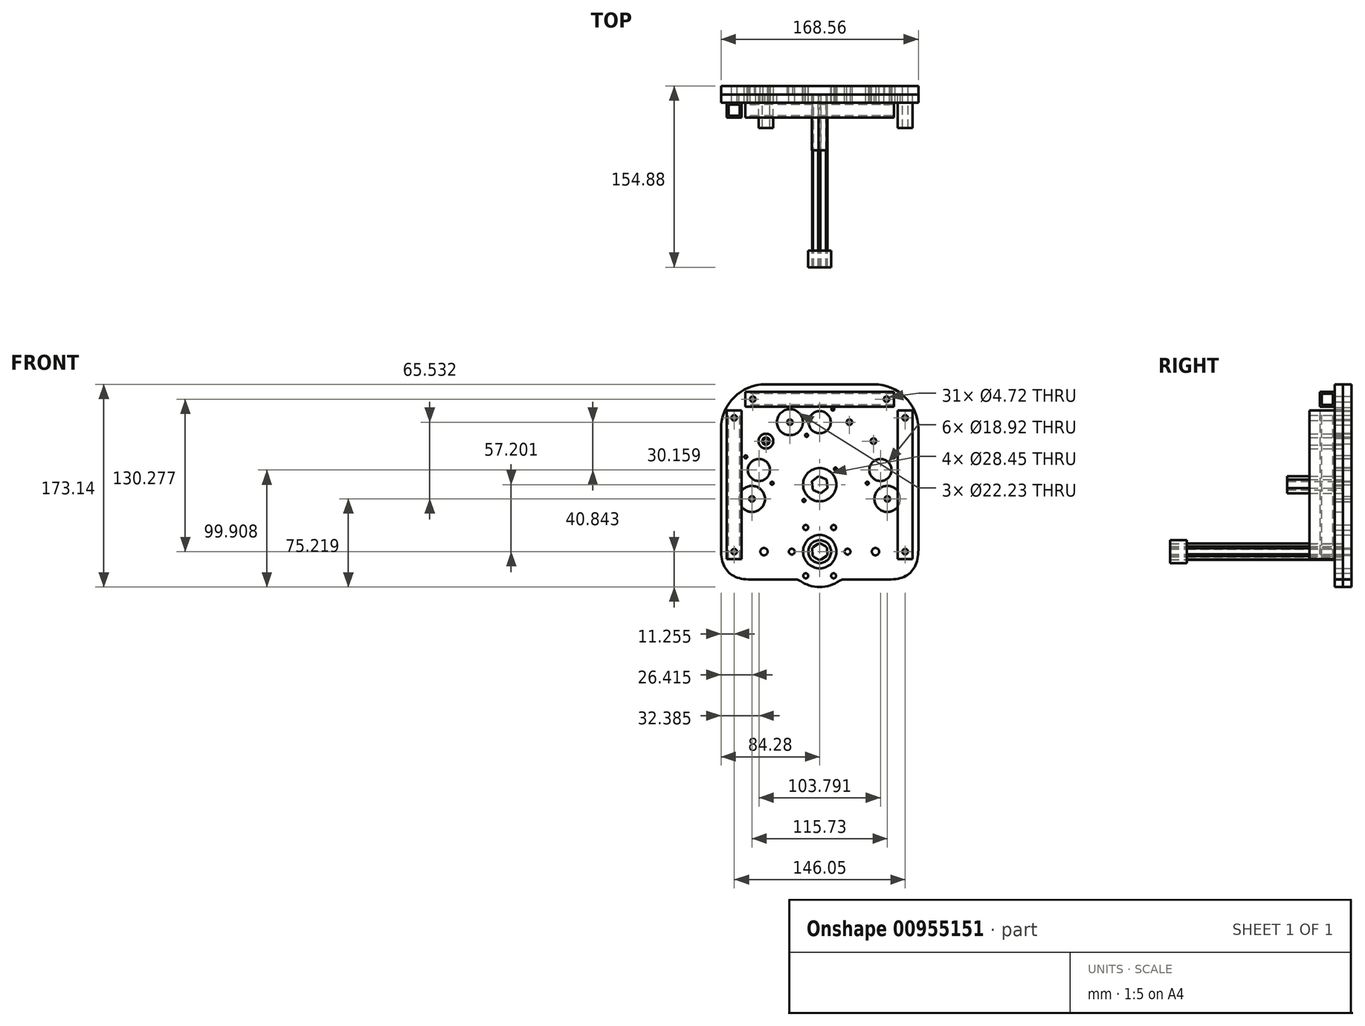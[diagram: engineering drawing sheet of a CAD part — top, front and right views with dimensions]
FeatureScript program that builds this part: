
annotation { "Feature Type Name" : "Feature", "Feature Type Description" : "" }
export const myFeature = defineFeature(function(context is Context, id is Id, definition is map)
    precondition{}
    {
        {
            var Q0;
            Q0=qCreatedBy(makeId("Front.planeOp"),FACE);
            var sketch = newSketch(context, id + "F0", { "sketchPlane" : qUnion([Q0])});
            skPoint(sketch, "E0.middle", {"position": v(0, 0) * mm});
            skCircle(sketch, "E1", {"center": v(0, 53.4) * mm, "radius": 9.46 * mm});
            skCircle(sketch, "E2", {"center": v(-51.9, 12.55) * mm, "radius": 9.46 * mm});
            skCircle(sketch, "E3", {"center": v(0, 0) * mm, "radius": 14.22 * mm});
            skCircle(sketch, "E4", {"center": v(0, -57.2) * mm, "radius": 14.22 * mm});
            skCircle(sketch, "E5", {"center": v(-25.4, 53.4) * mm, "radius": 2.36 * mm});
            skLineSegment(sketch, "E6", {"start": v(0, 0) * mm, "end": v(-51.9, 12.55) * mm, "construction": true});
            skLineSegment(sketch, "E7", {"start": v(-45.93, 37.24) * mm, "end": v(-57.86, -12.14) * mm, "construction": true});
            skCircle(sketch, "E8", {"center": v(-45.93, 37.24) * mm, "radius": 2.36 * mm});
            skCircle(sketch, "E9", {"center": v(-57.86, -12.14) * mm, "radius": 2.36 * mm});
            skCircle(sketch, "E10.MirrorC", {"center": v(45.93, 37.24) * mm, "radius": 2.36 * mm});
            skCircle(sketch, "E11.MirrorC", {"center": v(57.86, -12.14) * mm, "radius": 2.36 * mm});
            skCircle(sketch, "E12.MirrorC", {"center": v(25.4, 53.4) * mm, "radius": 2.36 * mm});
            skCircle(sketch, "E13.MirrorC", {"center": v(51.9, 12.55) * mm, "radius": 9.46 * mm});
            skCircle(sketch, "E14", {"center": v(-47.63, -57.2) * mm, "radius": 3.11 * mm});
            skCircle(sketch, "E15.MirrorC", {"center": v(47.63, -57.2) * mm, "radius": 3.11 * mm});
            skLineSegment(sketch, "E16", {"start": v(-25.4, 53.4) * mm, "end": v(25.4, 53.4) * mm, "construction": true});
            skCircle(sketch, "E17", {"center": v(0, 53.4) * mm, "radius": 32.39 * mm, "construction": true});
            skCircle(sketch, "E18", {"center": v(-51.9, 12.55) * mm, "radius": 32.39 * mm, "construction": true});
            skCircle(sketch, "E19", {"center": v(51.9, 12.55) * mm, "radius": 32.39 * mm, "construction": true});
            skLineSegment(sketch, "E20.bottom", {"start": v(84.28, 85.78) * mm, "end": v(-84.28, 85.78) * mm});
            skLineSegment(sketch, "E20.left", {"start": v(84.28, 85.78) * mm, "end": v(84.28, -81.01) * mm});
            skLineSegment(sketch, "E20.right", {"start": v(-84.28, 85.78) * mm, "end": v(-84.28, -81.01) * mm});
            skCircle(sketch, "E21", {"center": v(-73.03, 57.1) * mm, "radius": 2.36 * mm});
            skCircle(sketch, "E22.MirrorC", {"center": v(73.03, 57.1) * mm, "radius": 2.36 * mm});
            skCircle(sketch, "E23", {"center": v(-73.03, -57.2) * mm, "radius": 2.36 * mm});
            skCircle(sketch, "E24.MirrorC", {"center": v(73.03, -57.2) * mm, "radius": 2.36 * mm});
            skLineSegment(sketch, "E25", {"start": v(-11.23, 42.17) * mm, "end": v(11.23, 64.62) * mm, "construction": true});
            skCircle(sketch, "E26", {"center": v(-11.23, 42.17) * mm, "radius": 1.27 * mm});
            skCircle(sketch, "E27", {"center": v(11.23, 64.62) * mm, "radius": 1.27 * mm});
            skLineSegment(sketch, "E28", {"start": v(-57.15, 73.08) * mm, "end": v(57.15, 73.08) * mm, "construction": true});
            skCircle(sketch, "E29", {"center": v(-57.15, 73.08) * mm, "radius": 2.36 * mm});
            skLineSegment(sketch, "E30", {"start": v(-73.03, 57.1) * mm, "end": v(-73.03, -57.2) * mm, "construction": true});
            skPoint(sketch, "E31", {"position": v(0, 73.08) * mm});
            skCircle(sketch, "E32", {"center": v(57.15, 73.08) * mm, "radius": 2.36 * mm});
            skLineSegment(sketch, "E33", {"start": v(-13.47, -13.47) * mm, "end": v(13.47, 13.47) * mm, "construction": true});
            skCircle(sketch, "E34", {"center": v(13.47, 13.47) * mm, "radius": 1.27 * mm});
            skCircle(sketch, "E35", {"center": v(-13.47, -13.47) * mm, "radius": 1.27 * mm});
            skLineSegment(sketch, "E36", {"start": v(-63.12, 23.77) * mm, "end": v(-40.67, 1.32) * mm, "construction": true});
            skLineSegment(sketch, "E37", {"start": v(40.67, 1.32) * mm, "end": v(63.12, 23.77) * mm, "construction": true});
            skCircle(sketch, "E38", {"center": v(-40.67, 1.32) * mm, "radius": 1.27 * mm});
            skCircle(sketch, "E39", {"center": v(-63.12, 23.77) * mm, "radius": 1.27 * mm});
            skCircle(sketch, "E40", {"center": v(63.12, 23.77) * mm, "radius": 1.27 * mm});
            skCircle(sketch, "E41", {"center": v(40.67, 1.32) * mm, "radius": 1.27 * mm});
            skCircle(sketch, "E42", {"center": v(23.81, -57.2) * mm, "radius": 2.15 * mm});
            skCircle(sketch, "E43.1.0", {"center": v(11.9, -36.58) * mm, "radius": 2.15 * mm});
            skCircle(sketch, "E43.2.0", {"center": v(-11.9, -36.58) * mm, "radius": 2.15 * mm});
            skCircle(sketch, "E43.3.0", {"center": v(-23.81, -57.2) * mm, "radius": 2.15 * mm});
            skCircle(sketch, "E43.4.0", {"center": v(-11.9, -77.82) * mm, "radius": 2.15 * mm});
            skCircle(sketch, "E43.5.0", {"center": v(11.9, -77.82) * mm, "radius": 2.15 * mm});
            skCircle(sketch, "E44", {"center": v(0, -57.2) * mm, "radius": 23.81 * mm, "construction": true});
            skCircle(sketch, "E45.0", {"center": v(0, -57.2) * mm, "radius": 30.16 * mm, "construction": true});
            skLineSegment(sketch, "E46", {"start": v(84.28, -81.01) * mm, "end": v(18.51, -81.01) * mm});
            skLineSegment(sketch, "E47", {"start": v(-84.28, -81.01) * mm, "end": v(-18.51, -81.01) * mm});
            skArc(sketch, "E48", {"start": v(-18.51, -81.01) * mm, "mid": v(0, -87.36) * mm, "end": v(18.51, -81.01) * mm});
            skCircle(sketch, "E49", {"center": v(-23.81, -57.2) * mm, "radius": 2.49 * mm});
            skCircle(sketch, "E50", {"center": v(23.81, -57.2) * mm, "radius": 2.49 * mm});
            skSolve(sketch);
        }
        {
            var Q0;
            Q0=makeQuery(id+"F0.imprint","IMPRINT",FACE,{"disambiguationData":[TD([[makeQuery(id+"F0.imprint","IMPRINT",EDGE,{"derivedFrom":sQuery(id+"F0.wireOp",EDGE,"E1")}),-1.0]])]});
            extrude(context, id + "F1", {"entities" : qUnion([Q0]), "depth" : 7.24 * mm, "offsetDistance" : 25.4 * mm});
        }
        {
            var Q0;
            Q0=makeQuery(id+"F1.opExtrude","CAP_FACE",FACE,{"disambiguationData":[OSD([sQuery(id+"F0.wireOp",EDGE,"E1"),sQuery(id+"F0.wireOp",EDGE,"E2"),sQuery(id+"F0.wireOp",EDGE,"v2gbIf3F-sjIH-0Jlf-8SnF-WHDscdTQMHb3.bottom"),sQuery(id+"F0.wireOp",EDGE,"v2gbIf3F-sjIH-0Jlf-8SnF-WHDscdTQMHb3.top"),sQuery(id+"F0.wireOp",EDGE,"v2gbIf3F-sjIH-0Jlf-8SnF-WHDscdTQMHb3.left"),sQuery(id+"F0.wireOp",EDGE,"v2gbIf3F-sjIH-0Jlf-8SnF-WHDscdTQMHb3.right"),sQuery(id+"F0.wireOp",EDGE,"E3"),sQuery(id+"F0.wireOp",EDGE,"E4"),sQuery(id+"F0.wireOp",EDGE,"E5"),sQuery(id+"F0.wireOp",EDGE,"E8"),sQuery(id+"F0.wireOp",EDGE,"E9"),sQuery(id+"F0.wireOp",EDGE,"E10.MirrorC"),sQuery(id+"F0.wireOp",EDGE,"E11.MirrorC"),sQuery(id+"F0.wireOp",EDGE,"E12.MirrorC"),sQuery(id+"F0.wireOp",EDGE,"9f56034d-28e1-4162-898a-95c3412c0e040.MirrorCS"),sQuery(id+"F0.wireOp",EDGE,"273e83dc-7785-426b-80ec-8bf11da8723f0.MirrorCS"),sQuery(id+"F0.wireOp",EDGE,"E13.MirrorC")])],"isStart":false});
            var sketch = newSketch(context, id + "F2", { "sketchPlane" : qUnion([Q0])});
            skCircle(sketch, "E51", {"center": v(-45.93, 37.24) * mm, "radius": 6.35 * mm});
            skCircle(sketch, "E52", {"center": v(-45.93, 37.24) * mm, "radius": 3.18 * mm});
            skSolve(sketch);
        }
        {
            var Q0;
            Q0=qSketchRegion(id+"F2",true);
            extrude(context, id + "F3", {"entities" : qUnion([Q0]), "depth" : 28.75 * mm, "offsetDistance" : 25.4 * mm});
        }
        {
            var Q0;
            Q0=makeQuery(id+"F1.opExtrude","CAP_FACE",FACE,{"disambiguationData":[OSD([sQuery(id+"F0.wireOp",EDGE,"E1"),sQuery(id+"F0.wireOp",EDGE,"E2"),sQuery(id+"F0.wireOp",EDGE,"E3"),sQuery(id+"F0.wireOp",EDGE,"E4"),sQuery(id+"F0.wireOp",EDGE,"E5"),sQuery(id+"F0.wireOp",EDGE,"E8"),sQuery(id+"F0.wireOp",EDGE,"E9"),sQuery(id+"F0.wireOp",EDGE,"E10.MirrorC"),sQuery(id+"F0.wireOp",EDGE,"E11.MirrorC"),sQuery(id+"F0.wireOp",EDGE,"E12.MirrorC"),sQuery(id+"F0.wireOp",EDGE,"E13.MirrorC"),sQuery(id+"F0.wireOp",EDGE,"jZPg6kl5-KOBd-NjPk-bzl7-oyfRgCFlWvfu"),sQuery(id+"F0.wireOp",EDGE,"E14"),sQuery(id+"F0.wireOp",EDGE,"E15.MirrorC"),sQuery(id+"F0.wireOp",EDGE,"98a6a9db-e14f-428d-9856-ec1cbe78dd690.MirrorC"),sQuery(id+"F0.wireOp",EDGE,"E20.bottom"),sQuery(id+"F0.wireOp",EDGE,"E20.top"),sQuery(id+"F0.wireOp",EDGE,"E20.left"),sQuery(id+"F0.wireOp",EDGE,"E20.right"),sQuery(id+"F0.wireOp",EDGE,"E21"),sQuery(id+"F0.wireOp",EDGE,"E22.MirrorC"),sQuery(id+"F0.wireOp",EDGE,"E23"),sQuery(id+"F0.wireOp",EDGE,"E24.MirrorC")])],"isStart":false});
            var sketch = newSketch(context, id + "F4", { "sketchPlane" : qUnion([Q0])});
            skLineSegment(sketch, "E53.bottom", {"start": v(79.38, 63.45) * mm, "end": v(66.68, 63.45) * mm});
            skLineSegment(sketch, "E53.left", {"start": v(79.38, 63.45) * mm, "end": v(79.38, -63.55) * mm});
            skLineSegment(sketch, "E53.right", {"start": v(66.68, 63.45) * mm, "end": v(66.68, -63.55) * mm});
            skCircle(sketch, "E54", {"center": v(73.03, 57.1) * mm, "radius": 2.36 * mm});
            skCircle(sketch, "E55", {"center": v(73.03, -57.2) * mm, "radius": 2.36 * mm});
            skPoint(sketch, "E56", {"position": v(73.03, 63.45) * mm});
            skLineSegment(sketch, "E57", {"start": v(66.68, -63.55) * mm, "end": v(79.38, -63.55) * mm});
            skLineSegment(sketch, "E58", {"start": v(73.03, 63.45) * mm, "end": v(73.03, -63.55) * mm, "construction": true});
            skLineSegment(sketch, "E59", {"start": v(73.03, 57.1) * mm, "end": v(73.03, -57.2) * mm, "construction": true});
            skPoint(sketch, "E60", {"position": v(73.03, -0.05) * mm});
            skSolve(sketch);
        }
        {
            var Q0;
            Q0=qSketchRegion(id+"F4",true);
            var Q1;
            Q1=makeQuery(id+"F3.opExtrude","CAP_FACE",FACE,{"disambiguationData":[OSD([sQuery(id+"F2.wireOp",EDGE,"E51"),sQuery(id+"F2.wireOp",EDGE,"E52")])],"isStart":false});
            extrude(context, id + "F5", {"entities" : qUnion([Q0]), "endBound" : BoundingType.UP_TO_SURFACE, "depth" : 25.4 * mm, "endBoundEntityFace" : qUnion([Q1]), "offsetDistance" : 25.4 * mm});
        }
        {
            var Q0;
            Q0=makeQuery(id+"F1.opExtrude","CAP_FACE",FACE,{"disambiguationData":[OSD([sQuery(id+"F0.wireOp",EDGE,"E1"),sQuery(id+"F0.wireOp",EDGE,"E2"),sQuery(id+"F0.wireOp",EDGE,"E3"),sQuery(id+"F0.wireOp",EDGE,"E4"),sQuery(id+"F0.wireOp",EDGE,"E5"),sQuery(id+"F0.wireOp",EDGE,"E8"),sQuery(id+"F0.wireOp",EDGE,"E9"),sQuery(id+"F0.wireOp",EDGE,"E10.MirrorC"),sQuery(id+"F0.wireOp",EDGE,"E11.MirrorC"),sQuery(id+"F0.wireOp",EDGE,"E12.MirrorC"),sQuery(id+"F0.wireOp",EDGE,"E13.MirrorC"),sQuery(id+"F0.wireOp",EDGE,"E14"),sQuery(id+"F0.wireOp",EDGE,"E15.MirrorC"),sQuery(id+"F0.wireOp",EDGE,"E20.bottom"),sQuery(id+"F0.wireOp",EDGE,"E20.top"),sQuery(id+"F0.wireOp",EDGE,"E20.left"),sQuery(id+"F0.wireOp",EDGE,"E20.right"),sQuery(id+"F0.wireOp",EDGE,"E21"),sQuery(id+"F0.wireOp",EDGE,"E22.MirrorC"),sQuery(id+"F0.wireOp",EDGE,"E23"),sQuery(id+"F0.wireOp",EDGE,"E24.MirrorC"),sQuery(id+"F0.wireOp",EDGE,"E26"),sQuery(id+"F0.wireOp",EDGE,"E27"),sQuery(id+"F0.wireOp",EDGE,"E29"),sQuery(id+"F0.wireOp",EDGE,"E32")])],"isStart":false});
            var sketch = newSketch(context, id + "F6", { "sketchPlane" : qUnion([Q0])});
            skCircle(sketch, "E61.cCircle", {"center": v(0, 0) * mm, "radius": 6.35 * mm, "construction": true});
            skLineSegment(sketch, "E61.0", {"start": v(6.75, -2.87) * mm, "end": v(0.89, -7.28) * mm});
            skLineSegment(sketch, "E61.1", {"start": v(0.89, -7.28) * mm, "end": v(-5.86, -4.4) * mm});
            skLineSegment(sketch, "E61.2", {"start": v(-5.86, -4.4) * mm, "end": v(-6.75, 2.87) * mm});
            skLineSegment(sketch, "E61.3", {"start": v(-6.75, 2.87) * mm, "end": v(-0.89, 7.28) * mm});
            skLineSegment(sketch, "E61.4", {"start": v(-0.89, 7.28) * mm, "end": v(5.86, 4.4) * mm});
            skLineSegment(sketch, "E61.5", {"start": v(5.86, 4.4) * mm, "end": v(6.75, -2.87) * mm});
            skPoint(sketch, "E61.0.midPoint", {"position": v(3.82, -5.07) * mm});
            skSolve(sketch);
        }
        {
            var Q0;
            Q0=qSketchRegion(id+"F6",true);
            extrude(context, id + "F7", {"entities" : qUnion([Q0]), "depth" : 47.62 * mm, "offsetDistance" : 25.4 * mm});
        }
        {
            var Q0;
            Q0=makeQuery(id+"F1.opExtrude","CAP_FACE",FACE,{"disambiguationData":[OSD([sQuery(id+"F0.wireOp",EDGE,"E1"),sQuery(id+"F0.wireOp",EDGE,"E2"),sQuery(id+"F0.wireOp",EDGE,"E3"),sQuery(id+"F0.wireOp",EDGE,"E4"),sQuery(id+"F0.wireOp",EDGE,"E5"),sQuery(id+"F0.wireOp",EDGE,"E8"),sQuery(id+"F0.wireOp",EDGE,"E9"),sQuery(id+"F0.wireOp",EDGE,"E10.MirrorC"),sQuery(id+"F0.wireOp",EDGE,"E11.MirrorC"),sQuery(id+"F0.wireOp",EDGE,"E12.MirrorC"),sQuery(id+"F0.wireOp",EDGE,"E13.MirrorC"),sQuery(id+"F0.wireOp",EDGE,"E14"),sQuery(id+"F0.wireOp",EDGE,"E15.MirrorC"),sQuery(id+"F0.wireOp",EDGE,"E20.bottom"),sQuery(id+"F0.wireOp",EDGE,"E20.top"),sQuery(id+"F0.wireOp",EDGE,"E20.left"),sQuery(id+"F0.wireOp",EDGE,"E20.right"),sQuery(id+"F0.wireOp",EDGE,"E21"),sQuery(id+"F0.wireOp",EDGE,"E22.MirrorC"),sQuery(id+"F0.wireOp",EDGE,"E23"),sQuery(id+"F0.wireOp",EDGE,"E24.MirrorC"),sQuery(id+"F0.wireOp",EDGE,"E26"),sQuery(id+"F0.wireOp",EDGE,"E27"),sQuery(id+"F0.wireOp",EDGE,"E29"),sQuery(id+"F0.wireOp",EDGE,"E32")])],"isStart":false});
            var sketch = newSketch(context, id + "F8", { "sketchPlane" : qUnion([Q0])});
            skCircle(sketch, "E62.cCircle", {"center": v(0, -57.2) * mm, "radius": 6.35 * mm, "construction": true});
            skLineSegment(sketch, "E62.0", {"start": v(6.52, -60.55) * mm, "end": v(0.36, -64.52) * mm});
            skLineSegment(sketch, "E62.1", {"start": v(0.36, -64.52) * mm, "end": v(-6.16, -61.18) * mm});
            skLineSegment(sketch, "E62.2", {"start": v(-6.16, -61.18) * mm, "end": v(-6.52, -53.85) * mm});
            skLineSegment(sketch, "E62.3", {"start": v(-6.52, -53.85) * mm, "end": v(-0.36, -49.88) * mm});
            skLineSegment(sketch, "E62.4", {"start": v(-0.36, -49.88) * mm, "end": v(6.16, -53.22) * mm});
            skLineSegment(sketch, "E62.5", {"start": v(6.16, -53.22) * mm, "end": v(6.52, -60.55) * mm});
            skPoint(sketch, "E62.0.midPoint", {"position": v(3.44, -62.54) * mm});
            skCircle(sketch, "E63", {"center": v(0, -57.2) * mm, "radius": 6.88 * mm});
            skSolve(sketch);
        }
        {
            var Q0;
            {var subQ0=sQuery(id+"F8.wireOp",EDGE,"E63");var subQ14=sQuery(id+"F8.wireOp",EDGE,"E62.0");var subQ15=makeQuery(id+"F8.imprint","INTERSECT",VERTEX,{"disambiguationData":[OD(0.0)],"derivedFrom":[subQ14,subQ0]});Q0=makeQuery(id+"F8.imprint","IMPRINT",FACE,{"disambiguationData":[TD([[makeQuery(id+"F8.imprint","IMPRINT",EDGE,{"disambiguationData":[TD([[subQ15,-1.0]])],"derivedFrom":subQ14}),-1.0]])]});}
            extrude(context, id + "F9", {"entities" : qUnion([Q0]), "depth" : 133.35 * mm, "offsetDistance" : 25.4 * mm});
        }
        {
            var Q0;
            Q0=makeQuery(id+"F1.opExtrude","SWEPT_EDGE",EDGE,{"disambiguationData":[OSD([sQuery(id+"F0.wireOp",EDGE,"E20.left"),sQuery(id+"F0.wireOp",EDGE,"E46")])]});
            var Q1;
            Q1=makeQuery(id+"F1.opExtrude","SWEPT_EDGE",EDGE,{"disambiguationData":[OSD([sQuery(id+"F0.wireOp",EDGE,"E20.right"),sQuery(id+"F0.wireOp",EDGE,"E47")])]});
            fillet(context, id + "F10", {"entities" : qUnion([Q0, Q1]), "radius" : 25.4 * mm, "tangentPropagation" : true, "rho" : 0.5, "crossSection" : FilletCrossSection.CONIC, "allowEdgeOverflow" : false});
        }
        {
            var Q0;
            Q0=makeQuery(id+"F1.opExtrude","SWEPT_EDGE",EDGE,{"disambiguationData":[OSD([sQuery(id+"F0.wireOp",EDGE,"E47"),sQuery(id+"F0.wireOp",EDGE,"E48")])]});
            var Q1;
            Q1=makeQuery(id+"F1.opExtrude","SWEPT_EDGE",EDGE,{"disambiguationData":[OSD([sQuery(id+"F0.wireOp",EDGE,"E46"),sQuery(id+"F0.wireOp",EDGE,"E48")])]});
            fillet(context, id + "F11", {"entities" : qUnion([Q0, Q1]), "radius" : 6.35 * mm, "tangentPropagation" : true, "allowEdgeOverflow" : false});
        }
        {
            var Q0;
            Q0=makeQuery(id+"F1.opExtrude","SWEPT_EDGE",EDGE,{"disambiguationData":[OSD([sQuery(id+"F0.wireOp",EDGE,"E20.bottom"),sQuery(id+"F0.wireOp",EDGE,"E20.right")])]});
            var Q1;
            Q1=makeQuery(id+"F1.opExtrude","SWEPT_EDGE",EDGE,{"disambiguationData":[OSD([sQuery(id+"F0.wireOp",EDGE,"E20.bottom"),sQuery(id+"F0.wireOp",EDGE,"E20.left")])]});
            fillet(context, id + "F12", {"entities" : qUnion([Q0, Q1]), "radius" : 38.1 * mm, "tangentPropagation" : true, "allowEdgeOverflow" : false});
        }
        {
            var Q0;
            Q0=makeQuery(id+"F1.opExtrude","CAP_FACE",FACE,{"disambiguationData":[OSD([sQuery(id+"F0.wireOp",EDGE,"E1"),sQuery(id+"F0.wireOp",EDGE,"E2"),sQuery(id+"F0.wireOp",EDGE,"E3"),sQuery(id+"F0.wireOp",EDGE,"E4"),sQuery(id+"F0.wireOp",EDGE,"E5"),sQuery(id+"F0.wireOp",EDGE,"E8"),sQuery(id+"F0.wireOp",EDGE,"E9"),sQuery(id+"F0.wireOp",EDGE,"E10.MirrorC"),sQuery(id+"F0.wireOp",EDGE,"E11.MirrorC"),sQuery(id+"F0.wireOp",EDGE,"E12.MirrorC"),sQuery(id+"F0.wireOp",EDGE,"E13.MirrorC"),sQuery(id+"F0.wireOp",EDGE,"E14"),sQuery(id+"F0.wireOp",EDGE,"E15.MirrorC"),sQuery(id+"F0.wireOp",EDGE,"E20.bottom"),sQuery(id+"F0.wireOp",EDGE,"E20.left"),sQuery(id+"F0.wireOp",EDGE,"E20.right"),sQuery(id+"F0.wireOp",EDGE,"E21"),sQuery(id+"F0.wireOp",EDGE,"E22.MirrorC"),sQuery(id+"F0.wireOp",EDGE,"E23"),sQuery(id+"F0.wireOp",EDGE,"E24.MirrorC"),sQuery(id+"F0.wireOp",EDGE,"E26"),sQuery(id+"F0.wireOp",EDGE,"E27"),sQuery(id+"F0.wireOp",EDGE,"E29"),sQuery(id+"F0.wireOp",EDGE,"E32"),sQuery(id+"F0.wireOp",EDGE,"E34"),sQuery(id+"F0.wireOp",EDGE,"E35"),sQuery(id+"F0.wireOp",EDGE,"E38"),sQuery(id+"F0.wireOp",EDGE,"E39"),sQuery(id+"F0.wireOp",EDGE,"E40"),sQuery(id+"F0.wireOp",EDGE,"E41"),sQuery(id+"F0.wireOp",EDGE,"E42"),sQuery(id+"F0.wireOp",EDGE,"E43.1.0"),sQuery(id+"F0.wireOp",EDGE,"E43.2.0"),sQuery(id+"F0.wireOp",EDGE,"E43.3.0"),sQuery(id+"F0.wireOp",EDGE,"E43.4.0"),sQuery(id+"F0.wireOp",EDGE,"E43.5.0"),sQuery(id+"F0.wireOp",EDGE,"E46"),sQuery(id+"F0.wireOp",EDGE,"E47"),sQuery(id+"F0.wireOp",EDGE,"E48")])],"isStart":false});
            var sketch = newSketch(context, id + "F13", { "sketchPlane" : qUnion([Q0])});
            skCircle(sketch, "E64", {"center": v(-57.86, -12.14) * mm, "radius": 11.11 * mm});
            skCircle(sketch, "E65", {"center": v(57.86, -12.14) * mm, "radius": 11.11 * mm});
            skCircle(sketch, "E66", {"center": v(-25.4, 53.4) * mm, "radius": 11.11 * mm});
            skSolve(sketch);
        }
        {
            var Q0;
            Q0=makeQuery(id+"F13.imprint","IMPRINT",FACE,{"disambiguationData":[TD([[makeQuery(id+"F13.imprint","IMPRINT",EDGE,{"derivedFrom":sQuery(id+"F13.wireOp",EDGE,"E64")}),-1.0]])]});
            extrude(context, id + "F14", {"entities" : qUnion([Q0]), "depth" : 7.24 * mm, "offsetDistance" : 25.4 * mm});
        }
        {
            var Q0;
            Q0=makeQuery(id+"F14.opExtrude","CAP_FACE",FACE,{"disambiguationData":[OSD([sQuery(id+"F0.wireOp",EDGE,"E1"),sQuery(id+"F0.wireOp",EDGE,"E2"),sQuery(id+"F0.wireOp",EDGE,"E3"),sQuery(id+"F0.wireOp",EDGE,"E4"),sQuery(id+"F0.wireOp",EDGE,"E5"),sQuery(id+"F0.wireOp",EDGE,"E8"),sQuery(id+"F0.wireOp",EDGE,"E9"),sQuery(id+"F0.wireOp",EDGE,"E10.MirrorC"),sQuery(id+"F0.wireOp",EDGE,"E11.MirrorC"),sQuery(id+"F0.wireOp",EDGE,"E12.MirrorC"),sQuery(id+"F0.wireOp",EDGE,"E13.MirrorC"),sQuery(id+"F0.wireOp",EDGE,"E14"),sQuery(id+"F0.wireOp",EDGE,"E15.MirrorC"),sQuery(id+"F0.wireOp",EDGE,"E20.bottom"),sQuery(id+"F0.wireOp",EDGE,"E20.left"),sQuery(id+"F0.wireOp",EDGE,"E20.right"),sQuery(id+"F0.wireOp",EDGE,"E21"),sQuery(id+"F0.wireOp",EDGE,"E22.MirrorC"),sQuery(id+"F0.wireOp",EDGE,"E23"),sQuery(id+"F0.wireOp",EDGE,"E24.MirrorC"),sQuery(id+"F0.wireOp",EDGE,"E26"),sQuery(id+"F0.wireOp",EDGE,"E27"),sQuery(id+"F0.wireOp",EDGE,"E29"),sQuery(id+"F0.wireOp",EDGE,"E32"),sQuery(id+"F0.wireOp",EDGE,"E34"),sQuery(id+"F0.wireOp",EDGE,"E35"),sQuery(id+"F0.wireOp",EDGE,"E38"),sQuery(id+"F0.wireOp",EDGE,"E39"),sQuery(id+"F0.wireOp",EDGE,"E40"),sQuery(id+"F0.wireOp",EDGE,"E41"),sQuery(id+"F0.wireOp",EDGE,"E42"),sQuery(id+"F0.wireOp",EDGE,"E43.1.0"),sQuery(id+"F0.wireOp",EDGE,"E43.2.0"),sQuery(id+"F0.wireOp",EDGE,"E43.3.0"),sQuery(id+"F0.wireOp",EDGE,"E43.4.0"),sQuery(id+"F0.wireOp",EDGE,"E43.5.0"),sQuery(id+"F0.wireOp",EDGE,"E46"),sQuery(id+"F0.wireOp",EDGE,"E47"),sQuery(id+"F0.wireOp",EDGE,"E48"),sQuery(id+"F13.wireOp",EDGE,"E64"),sQuery(id+"F13.wireOp",EDGE,"E65"),sQuery(id+"F13.wireOp",EDGE,"E66")])],"isStart":false});
            var sketch = newSketch(context, id + "F15", { "sketchPlane" : qUnion([Q0])});
            skLineSegment(sketch, "E67.bottom", {"start": v(-79.38, 63.45) * mm, "end": v(-66.68, 63.45) * mm});
            skLineSegment(sketch, "E67.top", {"start": v(-79.38, -63.55) * mm, "end": v(-66.68, -63.55) * mm});
            skLineSegment(sketch, "E67.left", {"start": v(-79.38, 63.45) * mm, "end": v(-79.38, -63.55) * mm});
            skLineSegment(sketch, "E67.right", {"start": v(-66.68, 63.45) * mm, "end": v(-66.68, -63.55) * mm});
            skCircle(sketch, "E68", {"center": v(-73.03, 57.1) * mm, "radius": 2.36 * mm});
            skCircle(sketch, "E69", {"center": v(-73.03, -57.2) * mm, "radius": 2.36 * mm});
            skPoint(sketch, "E70", {"position": v(-73.03, 63.45) * mm});
            skSolve(sketch);
        }
        {
            var Q0;
            Q0=qSketchRegion(id+"F15",true);
            extrude(context, id + "F16", {"entities" : qUnion([Q0]), "depth" : 12.7 * mm, "offsetDistance" : 25.4 * mm});
        }
        {
            var Q0;
            Q0=makeQuery(id+"F14.opExtrude","CAP_FACE",FACE,{"disambiguationData":[OSD([sQuery(id+"F0.wireOp",EDGE,"E1"),sQuery(id+"F0.wireOp",EDGE,"E2"),sQuery(id+"F0.wireOp",EDGE,"E3"),sQuery(id+"F0.wireOp",EDGE,"E4"),sQuery(id+"F0.wireOp",EDGE,"E5"),sQuery(id+"F0.wireOp",EDGE,"E8"),sQuery(id+"F0.wireOp",EDGE,"E9"),sQuery(id+"F0.wireOp",EDGE,"E10.MirrorC"),sQuery(id+"F0.wireOp",EDGE,"E11.MirrorC"),sQuery(id+"F0.wireOp",EDGE,"E12.MirrorC"),sQuery(id+"F0.wireOp",EDGE,"E13.MirrorC"),sQuery(id+"F0.wireOp",EDGE,"E14"),sQuery(id+"F0.wireOp",EDGE,"E15.MirrorC"),sQuery(id+"F0.wireOp",EDGE,"E20.bottom"),sQuery(id+"F0.wireOp",EDGE,"E20.left"),sQuery(id+"F0.wireOp",EDGE,"E20.right"),sQuery(id+"F0.wireOp",EDGE,"E21"),sQuery(id+"F0.wireOp",EDGE,"E22.MirrorC"),sQuery(id+"F0.wireOp",EDGE,"E23"),sQuery(id+"F0.wireOp",EDGE,"E24.MirrorC"),sQuery(id+"F0.wireOp",EDGE,"E26"),sQuery(id+"F0.wireOp",EDGE,"E27"),sQuery(id+"F0.wireOp",EDGE,"E29"),sQuery(id+"F0.wireOp",EDGE,"E32"),sQuery(id+"F0.wireOp",EDGE,"E34"),sQuery(id+"F0.wireOp",EDGE,"E35"),sQuery(id+"F0.wireOp",EDGE,"E38"),sQuery(id+"F0.wireOp",EDGE,"E39"),sQuery(id+"F0.wireOp",EDGE,"E40"),sQuery(id+"F0.wireOp",EDGE,"E41"),sQuery(id+"F0.wireOp",EDGE,"E42"),sQuery(id+"F0.wireOp",EDGE,"E43.1.0"),sQuery(id+"F0.wireOp",EDGE,"E43.2.0"),sQuery(id+"F0.wireOp",EDGE,"E43.3.0"),sQuery(id+"F0.wireOp",EDGE,"E43.4.0"),sQuery(id+"F0.wireOp",EDGE,"E43.5.0"),sQuery(id+"F0.wireOp",EDGE,"E46"),sQuery(id+"F0.wireOp",EDGE,"E47"),sQuery(id+"F0.wireOp",EDGE,"E48"),sQuery(id+"F13.wireOp",EDGE,"E64"),sQuery(id+"F13.wireOp",EDGE,"E65"),sQuery(id+"F13.wireOp",EDGE,"E66")])],"isStart":false});
            var sketch = newSketch(context, id + "F17", { "sketchPlane" : qUnion([Q0])});
            skLineSegment(sketch, "E71.bottom", {"start": v(-63.5, 79.43) * mm, "end": v(63.5, 79.43) * mm});
            skLineSegment(sketch, "E71.top", {"start": v(-63.5, 66.73) * mm, "end": v(63.5, 66.73) * mm});
            skLineSegment(sketch, "E71.left", {"start": v(-63.5, 79.43) * mm, "end": v(-63.5, 66.73) * mm});
            skLineSegment(sketch, "E71.right", {"start": v(63.5, 79.43) * mm, "end": v(63.5, 66.73) * mm});
            skCircle(sketch, "E72", {"center": v(-57.15, 73.08) * mm, "radius": 2.36 * mm});
            skCircle(sketch, "E73", {"center": v(57.15, 73.08) * mm, "radius": 2.36 * mm});
            skPoint(sketch, "E74", {"position": v(-63.5, 73.08) * mm});
            skSolve(sketch);
        }
        {
            var Q0;
            Q0=qSketchRegion(id+"F17",true);
            extrude(context, id + "F18", {"entities" : qUnion([Q0]), "depth" : 12.7 * mm, "offsetDistance" : 25.4 * mm});
        }
        {
            var Q0;
            Q0=makeQuery(id+"F9.opExtrude","CAP_FACE",FACE,{"disambiguationData":[OSD([sQuery(id+"F8.wireOp",EDGE,"E62.0"),sQuery(id+"F8.wireOp",EDGE,"E62.1"),sQuery(id+"F8.wireOp",EDGE,"E62.2"),sQuery(id+"F8.wireOp",EDGE,"E62.3"),sQuery(id+"F8.wireOp",EDGE,"E62.4"),sQuery(id+"F8.wireOp",EDGE,"E62.5"),sQuery(id+"F8.wireOp",EDGE,"E63")])],"isStart":false});
            var sketch = newSketch(context, id + "F19", { "sketchPlane" : qUnion([Q0])});
            skCircle(sketch, "E75", {"center": v(0, -57.2) * mm, "radius": 9.75 * mm});
            skSolve(sketch);
        }
        {
            var Q0;
            Q0=makeQuery(id+"F19.imprint","IMPRINT",FACE,{"disambiguationData":[TD([[makeQuery(id+"F19.imprint","IMPRINT",EDGE,{"derivedFrom":sQuery(id+"F19.wireOp",EDGE,"E75")}),1.0]])]});
            extrude(context, id + "F20", {"entities" : qUnion([Q0]), "depth" : 14.29 * mm, "offsetDistance" : 25.4 * mm});
        }
        {
            var Q0;
            Q0=makeQuery(id+"F16.opExtrude","SWEPT_FACE",FACE,{"disambiguationData":[OSD([sQuery(id+"F15.wireOp",EDGE,"E67.bottom")])]});
            var sketch = newSketch(context, id + "F21", { "sketchPlane" : qUnion([Q0])});
            skLineSegment(sketch, "E76.0", {"start": v(-77.79, -25.6) * mm, "end": v(-77.79, -16.07) * mm});
            skLineSegment(sketch, "E76.1", {"start": v(-77.79, -25.6) * mm, "end": v(-68.26, -25.6) * mm});
            skLineSegment(sketch, "E76.2", {"start": v(-68.26, -25.6) * mm, "end": v(-68.26, -16.07) * mm});
            skLineSegment(sketch, "E76.3", {"start": v(-77.79, -16.07) * mm, "end": v(-68.26, -16.07) * mm});
            skSolve(sketch);
        }
        {
            var Q0;
            Q0=makeQuery(id+"F21.imprint","IMPRINT",FACE,{"disambiguationData":[TD([[makeQuery(id+"F21.imprint","IMPRINT",EDGE,{"derivedFrom":sQuery(id+"F21.wireOp",EDGE,"E76.0")}),-1.0]])]});
            var Q1;
            Q1=makeQuery(id+"F16.opExtrude","SWEPT_FACE",FACE,{"disambiguationData":[OSD([sQuery(id+"F15.wireOp",EDGE,"E67.top")])]});
            extrude(context, id + "F22", {"entities" : qUnion([Q0]), "operationType" : NewBodyOperationType.REMOVE, "endBound" : BoundingType.UP_TO_SURFACE, "oppositeDirection" : true, "depth" : 25.4 * mm, "endBoundEntityFace" : qUnion([Q1]), "offsetDistance" : 25.4 * mm});
        }
        {
            var Q0;
            Q0=makeQuery(id+"F18.opExtrude","SWEPT_FACE",FACE,{"disambiguationData":[OSD([sQuery(id+"F17.wireOp",EDGE,"E71.left")])]});
            var sketch = newSketch(context, id + "F23", { "sketchPlane" : qUnion([Q0])});
            skLineSegment(sketch, "E77.0", {"start": v(25.6, 68.31) * mm, "end": v(16.07, 68.31) * mm});
            skLineSegment(sketch, "E77.1", {"start": v(25.6, 77.84) * mm, "end": v(25.6, 68.31) * mm});
            skLineSegment(sketch, "E77.2", {"start": v(25.6, 77.84) * mm, "end": v(16.07, 77.84) * mm});
            skLineSegment(sketch, "E77.3", {"start": v(16.07, 77.84) * mm, "end": v(16.07, 68.31) * mm});
            skSolve(sketch);
        }
        {
            var Q0;
            Q0=makeQuery(id+"F23.imprint","IMPRINT",FACE,{"disambiguationData":[TD([[makeQuery(id+"F23.imprint","IMPRINT",EDGE,{"derivedFrom":sQuery(id+"F23.wireOp",EDGE,"E77.0")}),-1.0]])]});
            var Q1;
            Q1=makeQuery(id+"F18.opExtrude","SWEPT_FACE",FACE,{"disambiguationData":[OSD([sQuery(id+"F17.wireOp",EDGE,"E71.right")])]});
            extrude(context, id + "F24", {"entities" : qUnion([Q0]), "operationType" : NewBodyOperationType.REMOVE, "endBound" : BoundingType.UP_TO_SURFACE, "oppositeDirection" : true, "depth" : 25.4 * mm, "endBoundEntityFace" : qUnion([Q1]), "offsetDistance" : 25.4 * mm});
        }
    });
